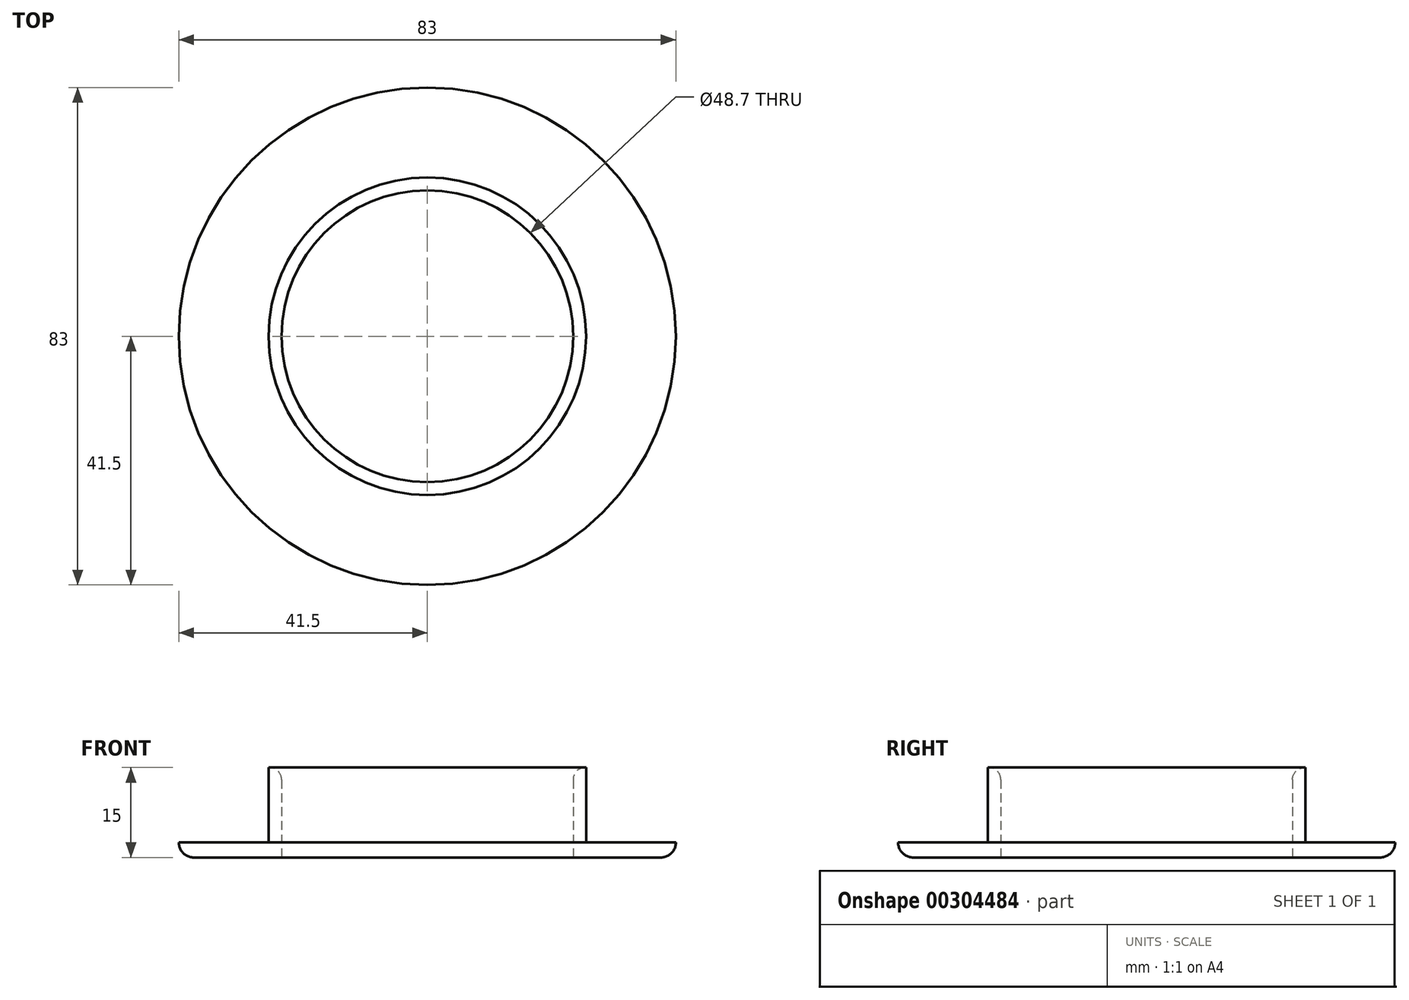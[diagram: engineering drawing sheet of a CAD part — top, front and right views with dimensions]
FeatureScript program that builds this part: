
annotation { "Feature Type Name" : "Feature", "Feature Type Description" : "" }
export const myFeature = defineFeature(function(context is Context, id is Id, definition is map)
    precondition{}
    {
        {
            var Q0;
            Q0=qCreatedBy(makeId("Top.planeOp"),FACE);
            var sketch = newSketch(context, id + "F0", { "sketchPlane" : qUnion([Q0])});
            skCircle(sketch, "E0", {"center": v(0, 0) * mm, "radius": 24.35 * mm});
            skCircle(sketch, "E1", {"center": v(0, 0) * mm, "radius": 41.5 * mm});
            skCircle(sketch, "E2", {"center": v(0, 0) * mm, "radius": 26.5 * mm});
            skSolve(sketch);
        }
        {
            var Q0;
            Q0=makeQuery(id+"F0.imprint","IMPRINT",FACE,{"disambiguationData":[TD([[makeQuery(id+"F0.imprint","IMPRINT",EDGE,{"derivedFrom":sQuery(id+"F0.wireOp",EDGE,"E1")}),1.0]])]});
            extrude(context, id + "F1", {"entities" : qUnion([Q0]), "depth" : 2.5 * mm});
        }
        {
            var Q0;
            Q0=makeQuery(id+"F0.imprint","IMPRINT",FACE,{"disambiguationData":[TD([[makeQuery(id+"F0.imprint","IMPRINT",EDGE,{"derivedFrom":sQuery(id+"F0.wireOp",EDGE,"E0")}),-1.0]])]});
            extrude(context, id + "F2", {"entities" : qUnion([Q0]), "operationType" : NewBodyOperationType.ADD, "depth" : 15 * mm});
        }
        {
            var Q0;
            Q0=makeQuery(id+"F1.opExtrude","CAP_EDGE",EDGE,{"disambiguationData":[OSD([sQuery(id+"F0.wireOp",EDGE,"E1")])],"isStart":true});
            fillet(context, id + "F3", {"entities" : qUnion([Q0]), "radius" : 2.5 * mm, "tangentPropagation" : true, "allowEdgeOverflow" : false});
        }
        {
            var Q0;
            Q0=makeQuery(id+"F2.opExtrude","CAP_EDGE",EDGE,{"disambiguationData":[OSD([sQuery(id+"F0.wireOp",EDGE,"E0")])],"isStart":false});
            fillet(context, id + "F4", {"entities" : qUnion([Q0]), "radius" : 2 * mm, "tangentPropagation" : true, "allowEdgeOverflow" : false});
        }
    });
